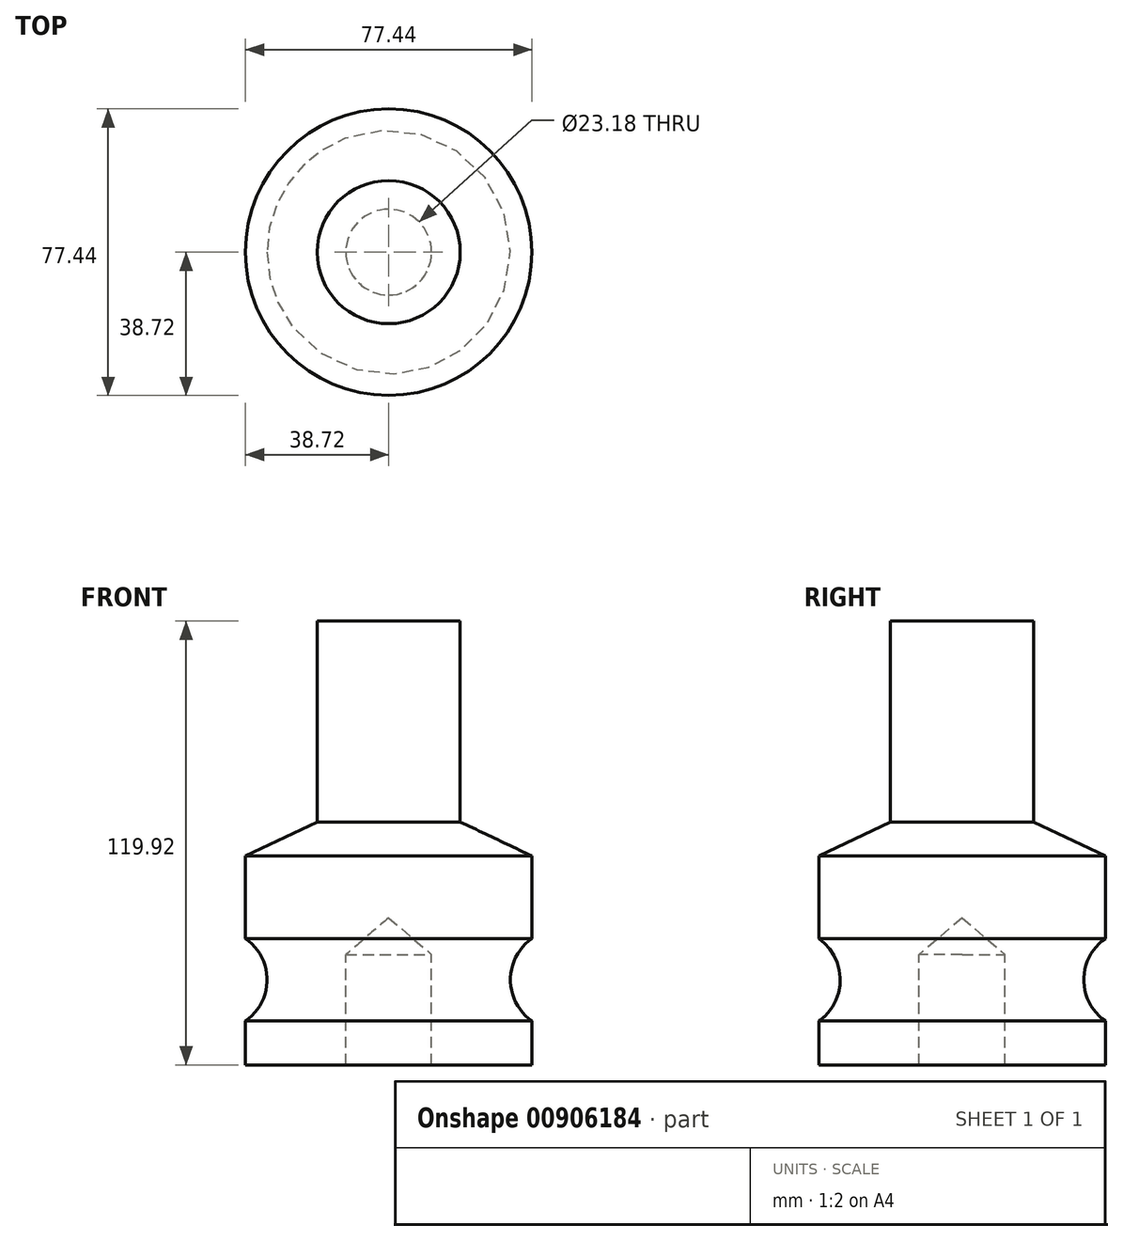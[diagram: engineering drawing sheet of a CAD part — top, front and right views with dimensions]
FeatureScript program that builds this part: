
annotation { "Feature Type Name" : "Feature", "Feature Type Description" : "" }
export const myFeature = defineFeature(function(context is Context, id is Id, definition is map)
    precondition{}
    {
        {
            var Q0;
            Q0=qCreatedBy(makeId("Front.planeOp"),FACE);
            var sketch = newSketch(context, id + "F0", { "sketchPlane" : qUnion([Q0])});
            skLineSegment(sketch, "E0.bottom", {"start": v(0, -12.96) * mm, "end": v(19.34, -12.96) * mm});
            skLineSegment(sketch, "E0.top", {"start": v(11.59, -132.88) * mm, "end": v(38.72, -132.88) * mm});
            skLineSegment(sketch, "E0.left", {"start": v(0, -12.96) * mm, "end": v(0, -93.15) * mm});
            skLineSegment(sketch, "E0.right", {"start": v(38.72, -76.43) * mm, "end": v(38.72, -132.88) * mm});
            skLineSegment(sketch, "E1", {"start": v(38.72, -76.43) * mm, "end": v(19.34, -67.23) * mm});
            skLineSegment(sketch, "E2", {"start": v(19.34, -67.23) * mm, "end": v(19.34, -12.96) * mm});
            skLineSegment(sketch, "E3", {"start": v(11.59, -132.88) * mm, "end": v(11.59, -103.08) * mm});
            skLineSegment(sketch, "E4", {"start": v(11.59, -103.08) * mm, "end": v(0, -93.15) * mm});
            skCircle(sketch, "E5", {"center": v(46.48, -109.87) * mm, "radius": 13.58 * mm});
            skSolve(sketch);
        }
        {
            var Q0;
            Q0=makeQuery(id+"F0.imprint","IMPRINT",FACE,{"disambiguationData":[TD([[makeQuery(id+"F0.imprint","IMPRINT",EDGE,{"derivedFrom":sQuery(id+"F0.wireOp",EDGE,"E0.bottom")}),-1.0]])]});
            var Q1;
            {var subQ0=sQuery(id+"F0.wireOp",EDGE,"E5");var subQ1=sQuery(id+"F0.wireOp",EDGE,"E0.right");var subQ2=makeQuery(id+"F0.imprint","INTERSECT",VERTEX,{"disambiguationData":[OD(0.0)],"derivedFrom":[subQ1,subQ0]});Q1=makeQuery(id+"F0.imprint","IMPRINT",FACE,{"disambiguationData":[TD([[makeQuery(id+"F0.imprint","IMPRINT",EDGE,{"disambiguationData":[TD([[subQ2,-1.0]])],"derivedFrom":subQ1}),-1.0]])]});}
            var Q2;
            Q2=sQuery(id+"F0.wireOp",EDGE,"E0.left");
            revolve(context, id + "F1", {"surfaceOperationType" : NewSurfaceOperationType.NEW, "entities" : qUnion([Q0, Q1]), "axis" : qUnion([Q2]), "revolveType" : RevolveType.FULL});
        }
        {
            var Q0;
            {var subQ0=sQuery(id+"F0.wireOp",EDGE,"E5");var subQ1=sQuery(id+"F0.wireOp",EDGE,"E0.right");var subQ2=makeQuery(id+"F0.imprint","INTERSECT",VERTEX,{"disambiguationData":[OD(0.0)],"derivedFrom":[subQ1,subQ0]});Q0=makeQuery(id+"F0.imprint","IMPRINT",FACE,{"disambiguationData":[TD([[makeQuery(id+"F0.imprint","IMPRINT",EDGE,{"disambiguationData":[TD([[subQ2,-1.0]])],"derivedFrom":subQ1}),-1.0]])]});}
            var Q1;
            Q1=sQuery(id+"F0.wireOp",EDGE,"E0.left");
            revolve(context, id + "F2", {"operationType" : NewBodyOperationType.REMOVE, "surfaceOperationType" : NewSurfaceOperationType.NEW, "entities" : qUnion([Q0]), "axis" : qUnion([Q1]), "revolveType" : RevolveType.FULL, "oppositeDirection" : true});
        }
    });
